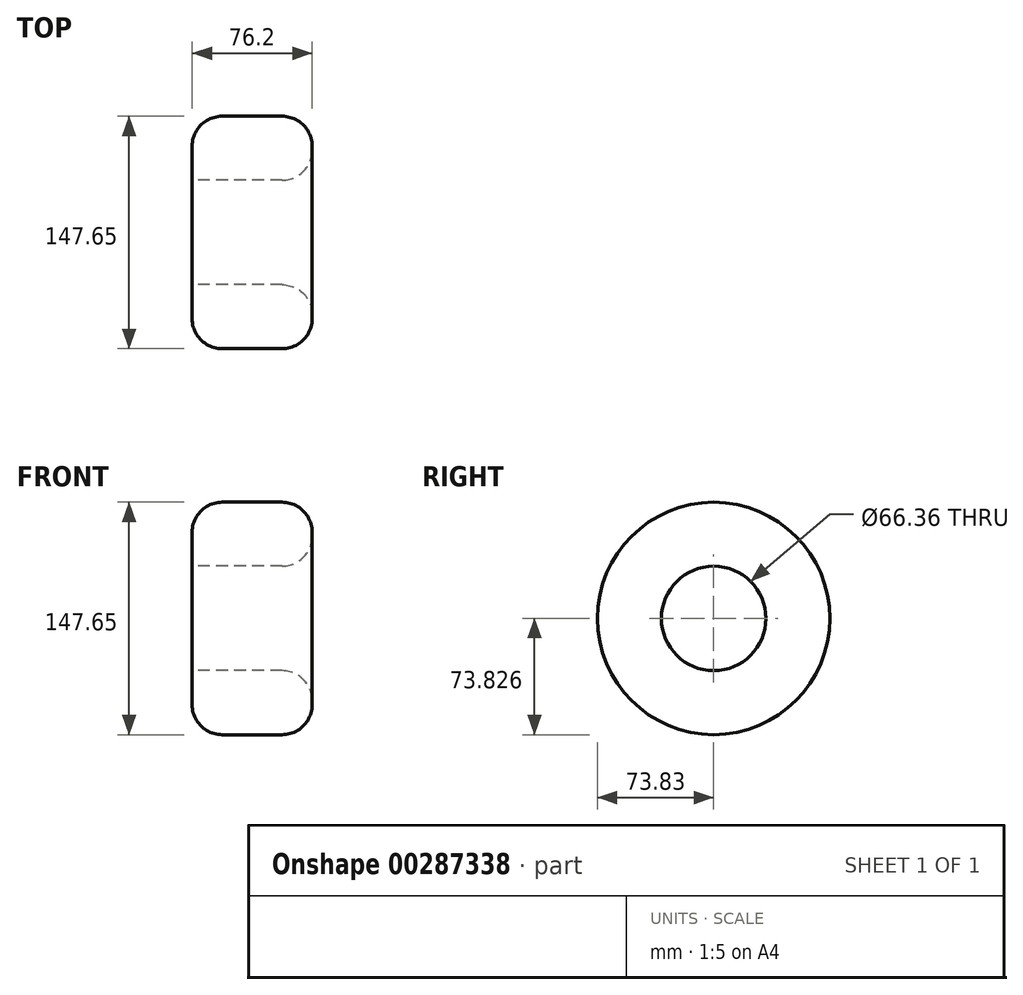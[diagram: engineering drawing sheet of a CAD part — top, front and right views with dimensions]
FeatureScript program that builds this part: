
annotation { "Feature Type Name" : "Feature", "Feature Type Description" : "" }
export const myFeature = defineFeature(function(context is Context, id is Id, definition is map)
    precondition{}
    {
        {
            var Q0;
            Q0=qCreatedBy(makeId("Right.planeOp"),FACE);
            var sketch = newSketch(context, id + "F0", { "sketchPlane" : qUnion([Q0])});
            skCircle(sketch, "E0", {"center": v(-26.87, 9.45) * mm, "radius": 73.82 * mm});
            skCircle(sketch, "E1", {"center": v(-26.87, 9.45) * mm, "radius": 33.18 * mm});
            skSolve(sketch);
        }
        {
            var Q0;
            Q0=makeQuery(id+"F0.imprint","IMPRINT",FACE,{"disambiguationData":[TD([[makeQuery(id+"F0.imprint","IMPRINT",EDGE,{"derivedFrom":sQuery(id+"F0.wireOp",EDGE,"E0")}),1.0]])]});
            extrude(context, id + "F1", {"entities" : qUnion([Q0]), "depth" : 76.2 * mm});
        }
        {
            var Q0;
            Q0=makeQuery(id+"F1.opExtrude","SWEPT_FACE",FACE,{"disambiguationData":[OSD([sQuery(id+"F0.wireOp",EDGE,"E0")])]});
            var Q1;
            Q1=makeQuery(id+"F1.opExtrude","CAP_FACE",FACE,{"disambiguationData":[OSD([sQuery(id+"F0.wireOp",EDGE,"E0"),sQuery(id+"F0.wireOp",EDGE,"E1")])],"isStart":false});
            fillet(context, id + "F2", {"entities" : qUnion([Q0, Q1]), "radius" : 19.05 * mm, "tangentPropagation" : true, "allowEdgeOverflow" : false});
        }
    });
